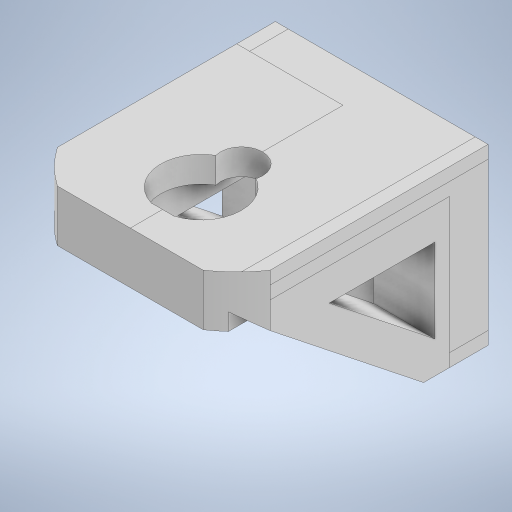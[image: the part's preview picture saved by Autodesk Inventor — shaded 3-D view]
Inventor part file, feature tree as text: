
AUTODESK INVENTOR PART (.ipt)
format: ipt  version: 2024 (Build 280153000, 153)  size: 678,400 bytes
history: native  units: mm
features: extrude x9, reference x6, projected_geometry x5, other x5, sketch x3, plane x2, mirror x1
ambient origin geometry x8: Origin, YZ Plane, XZ Plane, XY Plane, X Axis, Y Axis, Z Axis, Center Point
bodies: Solid1 (feature_tree)
feature tree (31):
  plane  "Work Plane1"
  extrude  "Extrusion1"  Depth=4.0mm
  extrude  "Extrusion7"  Depth=11.0mm
  extrude  "Extrusion9"  Depth=10.0mm
  extrude  "Extrusion8"  Depth=10.0mm
  extrude  "Extrusion10"  Depth=10.0mm
  extrude  "Extrusion11"  Depth=10.0mm
  plane  "Work Plane3"
  mirror  "Mirror3"
  extrude  "Extrusion12"  Depth=10.0mm
  extrude  "Extrusion13"  Depth=10.0mm
  extrude  "Extrusion15"  Depth=10.0mm
  reference  "Reference1"
  reference  "Reference2"
  reference  "Reference3"
  reference  "Reference4"
  reference  "Reference5"
  reference  "Reference6"
  projected_geometry  "Projected Loop4"
  projected_geometry  "Projected Loop5"
  sketch  "Sketch15"  dims[d0=6.0mm d1=0.0mm d42=4.0mm]
  projected_geometry  "Projected Loop6"
  sketch  "Sketch16"  dims[d43=33.0mm d44=0.0mm d46=11.0mm]
  projected_geometry  "Projected Loop7"
  projected_geometry  "Projected Loop8"
  sketch  "Sketch18"  dims[d47=12.5mm d48=6.5mm d49=14.0mm d50=5.0mm d51=2.5mm d52=16.5mm d53=2.5mm d54=16.5mm d55=4.0mm d56=0.0mm d57=0.0mm d58=0.0mm d59=3.0mm d60=3.0mm d61=20.0mm d62=0.0mm d65=4.0mm d66=0.0mm d67=-16.5mm d89=10.0mm d90=5.0mm d91=10.0mm d92=0.0mm d93=0.0mm d94=0.0mm d111=40.0mm d112=22.500017mm d113=10.0mm d114=0.0mm d30=0.5mm d31=0.872665mm d32=0.5mm d33=0.872665mm d95=0.5mm d96=0.872665mm d107=0.0mm d108=0.0mm d109=0.0mm d110=0.0mm]
  other  "<userpath> windows\Documents\Inventor\Robotska_roka\Assembly4.iam"
  other  "Assembly4.iam"
  other  "SG90 - Micro Servo 9g - Tower Pro:1"
  other  "SG90 - Micro Servo 9g - Tower Pro.4"
  other  "roka2:1"
